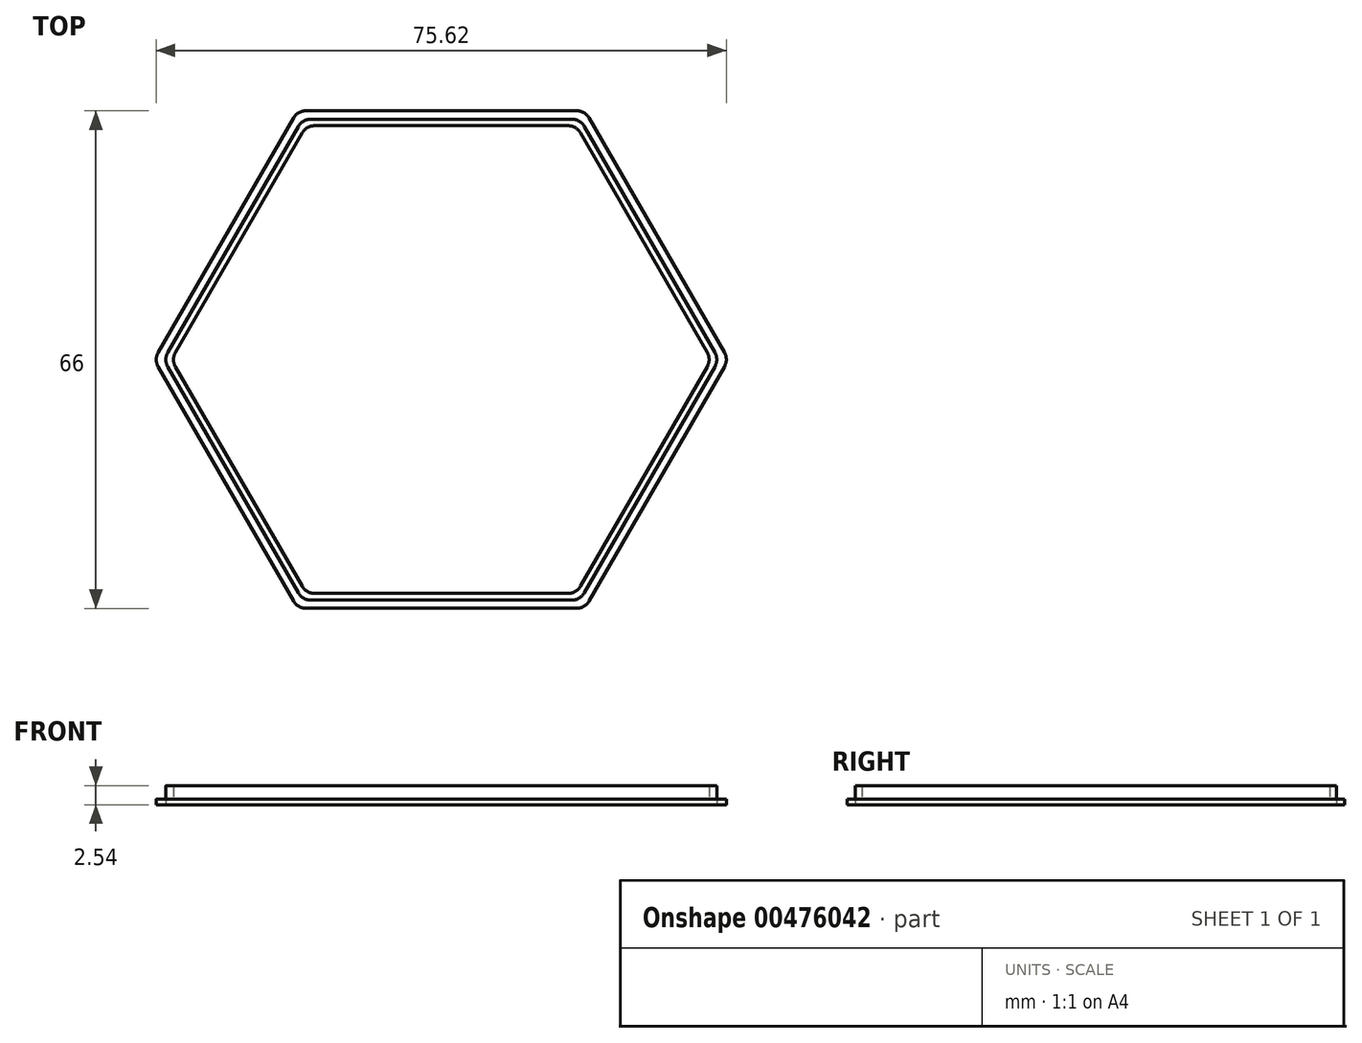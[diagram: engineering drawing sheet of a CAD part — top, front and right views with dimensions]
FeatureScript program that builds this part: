
annotation { "Feature Type Name" : "Feature", "Feature Type Description" : "" }
export const myFeature = defineFeature(function(context is Context, id is Id, definition is map)
    precondition{}
    {
        {
            var Q0;
            Q0=qCreatedBy(makeId("Top.planeOp"),FACE);
            var sketch = newSketch(context, id + "F0", { "sketchPlane" : qUnion([Q0])});
            skLineSegment(sketch, "E0", {"start": v(-56.1, -68.55) * mm, "end": v(58.07, -68.55) * mm});
            skLineSegment(sketch, "E1", {"start": v(0, 0) * mm, "end": v(-19.05, 33) * mm, "construction": true});
            skLineSegment(sketch, "E2", {"start": v(19.05, 33) * mm, "end": v(0, 0) * mm, "construction": true});
            skLineSegment(sketch, "E3", {"start": v(-19.05, 33) * mm, "end": v(19.05, 33) * mm});
            skLineSegment(sketch, "E4.1.0", {"start": v(-38.1, 0) * mm, "end": v(-19.05, 33) * mm});
            skLineSegment(sketch, "E4.2.0", {"start": v(-19.05, -33) * mm, "end": v(-38.1, 0) * mm});
            skLineSegment(sketch, "E4.3.0", {"start": v(19.05, -33) * mm, "end": v(-19.05, -33) * mm});
            skLineSegment(sketch, "E4.4.0", {"start": v(38.1, 0) * mm, "end": v(19.05, -33) * mm});
            skLineSegment(sketch, "E4.5.0", {"start": v(19.05, 33) * mm, "end": v(38.1, 0) * mm});
            skPoint(sketch, "E4.center", {"position": v(0, 0) * mm});
            skSolve(sketch);
        }
        {
            var Q0;
            Q0=makeQuery(id+"F0.imprint","IMPRINT",FACE,{"disambiguationData":[TD([[makeQuery(id+"F0.imprint","IMPRINT",EDGE,{"derivedFrom":sQuery(id+"F0.wireOp",EDGE,"E3")}),-1.0]])]});
            extrude(context, id + "F1", {"entities" : qUnion([Q0]), "depth" : 0.76 * mm, "offsetDistance" : 25.4 * mm});
        }
        {
            var Q0;
            Q0=makeQuery(id+"FdZoSmRdGPEDfu0_1.splitOp","SPLIT",EDGE,{"derivedFrom":makeQuery(id+"F1.opExtrude","SWEPT_EDGE",EDGE,{"disambiguationData":[OSD([sQuery(id+"F0.wireOp",EDGE,"E4.4.0"),sQuery(id+"F0.wireOp",EDGE,"E4.5.0")])]})});
            var Q1;
            Q1=makeQuery(id+"FdZoSmRdGPEDfu0_1.splitOp","SPLIT",EDGE,{"derivedFrom":makeQuery(id+"F1.opExtrude","SWEPT_EDGE",EDGE,{"disambiguationData":[OSD([sQuery(id+"F0.wireOp",EDGE,"E3"),sQuery(id+"F0.wireOp",EDGE,"E4.5.0")])]})});
            var Q2;
            Q2=makeQuery(id+"FdZoSmRdGPEDfu0_1.splitOp","SPLIT",EDGE,{"derivedFrom":makeQuery(id+"F1.opExtrude","SWEPT_EDGE",EDGE,{"disambiguationData":[OSD([sQuery(id+"F0.wireOp",EDGE,"E3"),sQuery(id+"F0.wireOp",EDGE,"E4.1.0")])]})});
            var Q3;
            Q3=makeQuery(id+"FdZoSmRdGPEDfu0_1.splitOp","SPLIT",EDGE,{"derivedFrom":makeQuery(id+"F1.opExtrude","SWEPT_EDGE",EDGE,{"disambiguationData":[OSD([sQuery(id+"F0.wireOp",EDGE,"E4.1.0"),sQuery(id+"F0.wireOp",EDGE,"E4.2.0")])]})});
            var Q4;
            Q4=makeQuery(id+"FdZoSmRdGPEDfu0_1.splitOp","SPLIT",EDGE,{"derivedFrom":makeQuery(id+"F1.opExtrude","SWEPT_EDGE",EDGE,{"disambiguationData":[OSD([sQuery(id+"F0.wireOp",EDGE,"E4.2.0"),sQuery(id+"F0.wireOp",EDGE,"E4.3.0")])]})});
            var Q5;
            Q5=makeQuery(id+"FdZoSmRdGPEDfu0_1.splitOp","SPLIT",EDGE,{"derivedFrom":makeQuery(id+"F1.opExtrude","SWEPT_EDGE",EDGE,{"disambiguationData":[OSD([sQuery(id+"F0.wireOp",EDGE,"E4.3.0"),sQuery(id+"F0.wireOp",EDGE,"E4.4.0")])]})});
            fillet(context, id + "F2", {"entities" : qUnion([Q0, Q1, Q2, Q3, Q4, Q5]), "radius" : 1.9 * mm, "allowEdgeOverflow" : false});
        }
        {
            var Q0;
            Q0=qCreatedBy(makeId("Top.planeOp"),FACE);
            var sketch = newSketch(context, id + "F3", { "sketchPlane" : qUnion([Q0])});
            skLineSegment(sketch, "E5", {"start": v(0, 0) * mm, "end": v(-18.41, 31.9) * mm, "construction": true});
            skLineSegment(sketch, "E6", {"start": v(0, 0) * mm, "end": v(18.41, 31.9) * mm, "construction": true});
            skLineSegment(sketch, "E7", {"start": v(-18.41, 31.9) * mm, "end": v(18.41, 31.9) * mm});
            skLineSegment(sketch, "E8.1.0", {"start": v(-36.83, 0) * mm, "end": v(-18.41, 31.9) * mm});
            skLineSegment(sketch, "E8.2.0", {"start": v(-18.42, -31.9) * mm, "end": v(-36.83, 0) * mm});
            skLineSegment(sketch, "E8.3.0", {"start": v(18.41, -31.9) * mm, "end": v(-18.41, -31.9) * mm});
            skLineSegment(sketch, "E8.4.0", {"start": v(36.83, 0) * mm, "end": v(18.41, -31.9) * mm});
            skLineSegment(sketch, "E8.5.0", {"start": v(18.41, 31.9) * mm, "end": v(36.83, 0) * mm});
            skPoint(sketch, "E8.center", {"position": v(0, 0) * mm});
            skSolve(sketch);
        }
        {
            var Q0;
            Q0=qSketchRegion(id+"F3",true);
            extrude(context, id + "F4", {"entities" : qUnion([Q0]), "depth" : 2.54 * mm, "offsetDistance" : 25.4 * mm});
        }
        {
            var Q0;
            Q0=makeQuery(id+"F4.opExtrude","SWEPT_EDGE",EDGE,{"disambiguationData":[OSD([sQuery(id+"F3.wireOp",EDGE,"E8.2.0"),sQuery(id+"F3.wireOp",EDGE,"E8.3.0")])]});
            var Q1;
            Q1=makeQuery(id+"F4.opExtrude","SWEPT_EDGE",EDGE,{"disambiguationData":[OSD([sQuery(id+"F3.wireOp",EDGE,"E8.3.0"),sQuery(id+"F3.wireOp",EDGE,"E8.4.0")])]});
            var Q2;
            Q2=makeQuery(id+"F4.opExtrude","SWEPT_EDGE",EDGE,{"disambiguationData":[OSD([sQuery(id+"F3.wireOp",EDGE,"E8.4.0"),sQuery(id+"F3.wireOp",EDGE,"E8.5.0")])]});
            var Q3;
            Q3=makeQuery(id+"F4.opExtrude","SWEPT_EDGE",EDGE,{"disambiguationData":[OSD([sQuery(id+"F3.wireOp",EDGE,"E8.1.0"),sQuery(id+"F3.wireOp",EDGE,"E8.2.0")])]});
            var Q4;
            Q4=makeQuery(id+"F4.opExtrude","SWEPT_EDGE",EDGE,{"disambiguationData":[OSD([sQuery(id+"F3.wireOp",EDGE,"E7"),sQuery(id+"F3.wireOp",EDGE,"E8.5.0")])]});
            var Q5;
            Q5=makeQuery(id+"F4.opExtrude","SWEPT_EDGE",EDGE,{"disambiguationData":[OSD([sQuery(id+"F3.wireOp",EDGE,"E7"),sQuery(id+"F3.wireOp",EDGE,"E8.1.0")])]});
            fillet(context, id + "F5", {"entities" : qUnion([Q0, Q1, Q2, Q3, Q4, Q5]), "radius" : 1.9 * mm, "tangentPropagation" : true, "allowEdgeOverflow" : false});
        }
        {
            var Q0;
            Q0=qCreatedBy(makeId("Top.planeOp"),FACE);
            var sketch = newSketch(context, id + "F6", { "sketchPlane" : qUnion([Q0])});
            skLineSegment(sketch, "E9", {"start": v(-17.9, 31.02) * mm, "end": v(0, 0) * mm, "construction": true});
            skLineSegment(sketch, "E10", {"start": v(0, 0) * mm, "end": v(17.9, 31.02) * mm, "construction": true});
            skLineSegment(sketch, "E11", {"start": v(-17.9, 31.02) * mm, "end": v(17.9, 31.02) * mm});
            skLineSegment(sketch, "E12.1.0", {"start": v(-35.81, 0) * mm, "end": v(-17.9, 31.02) * mm});
            skLineSegment(sketch, "E12.2.0", {"start": v(-17.9, -31.02) * mm, "end": v(-35.81, 0) * mm});
            skLineSegment(sketch, "E12.3.0", {"start": v(17.9, -31.02) * mm, "end": v(-17.9, -31.02) * mm});
            skLineSegment(sketch, "E12.4.0", {"start": v(35.81, 0) * mm, "end": v(17.9, -31.02) * mm});
            skLineSegment(sketch, "E12.5.0", {"start": v(17.9, 31.02) * mm, "end": v(35.81, 0) * mm});
            skPoint(sketch, "E12.center", {"position": v(0, 0) * mm});
            skSolve(sketch);
        }
        {
            var Q0;
            Q0 = qSketchRegion(id + "F6", true);
            extrude(context, id + "F7", {"entities" : qUnion([Q0]), "depth" : 2.54 * mm, "offsetDistance" : 25.4 * mm});
        }
        {
            var Q0;
            Q0=makeQuery(id+"F7.opExtrude","SWEPT_EDGE",EDGE,{"disambiguationData":[OSD([sQuery(id+"F6.wireOp",EDGE,"E12.2.0"),sQuery(id+"F6.wireOp",EDGE,"E12.3.0")])]});
            var Q1;
            Q1=makeQuery(id+"F7.opExtrude","SWEPT_EDGE",EDGE,{"disambiguationData":[OSD([sQuery(id+"F6.wireOp",EDGE,"E12.3.0"),sQuery(id+"F6.wireOp",EDGE,"E12.4.0")])]});
            var Q2;
            Q2=makeQuery(id+"F7.opExtrude","SWEPT_EDGE",EDGE,{"disambiguationData":[OSD([sQuery(id+"F6.wireOp",EDGE,"E12.4.0"),sQuery(id+"F6.wireOp",EDGE,"E12.5.0")])]});
            var Q3;
            Q3=makeQuery(id+"F7.opExtrude","SWEPT_EDGE",EDGE,{"disambiguationData":[OSD([sQuery(id+"F6.wireOp",EDGE,"E12.1.0"),sQuery(id+"F6.wireOp",EDGE,"E12.2.0")])]});
            var Q4;
            Q4=makeQuery(id+"F7.opExtrude","SWEPT_EDGE",EDGE,{"disambiguationData":[OSD([sQuery(id+"F6.wireOp",EDGE,"E11"),sQuery(id+"F6.wireOp",EDGE,"E12.5.0")])]});
            var Q5;
            Q5=makeQuery(id+"F7.opExtrude","SWEPT_EDGE",EDGE,{"disambiguationData":[OSD([sQuery(id+"F6.wireOp",EDGE,"E11"),sQuery(id+"F6.wireOp",EDGE,"E12.1.0")])]});
            fillet(context, id + "F8", {"entities" : qUnion([Q0, Q1, Q2, Q3, Q4, Q5]), "radius" : 1.9 * mm, "tangentPropagation" : true, "allowEdgeOverflow" : false});
        }
        {
            var Q0;
            Q0=makeQuery(id+"F7.opExtrude","SWEPT_BODY",BODY,{"disambiguationData":[OSD([sQuery(id+"F6.wireOp",EDGE,"E11"),sQuery(id+"F6.wireOp",EDGE,"E12.1.0"),sQuery(id+"F6.wireOp",EDGE,"E12.2.0"),sQuery(id+"F6.wireOp",EDGE,"E12.3.0"),sQuery(id+"F6.wireOp",EDGE,"E12.4.0"),sQuery(id+"F6.wireOp",EDGE,"E12.5.0")])]});
            transform(context, id + "F9", {"entities" : qUnion([Q0]), "transformType" : TransformType.TRANSLATION_3D, "dx" : 0 * mm, "dy" : 0 * mm, "dz" : 0.76 * mm, "makeCopy" : false});
        }
        {
            var Q0;
            Q0=makeQuery(id+"F7.opExtrude","SWEPT_BODY",BODY,{"disambiguationData":[OSD([sQuery(id+"F6.wireOp",EDGE,"E11"),sQuery(id+"F6.wireOp",EDGE,"E12.1.0"),sQuery(id+"F6.wireOp",EDGE,"E12.2.0"),sQuery(id+"F6.wireOp",EDGE,"E12.3.0"),sQuery(id+"F6.wireOp",EDGE,"E12.4.0"),sQuery(id+"F6.wireOp",EDGE,"E12.5.0")])]});
            var Q1;
            Q1=makeQuery(id+"F4.opExtrude","SWEPT_BODY",BODY,{"disambiguationData":[OSD([sQuery(id+"F3.wireOp",EDGE,"E7"),sQuery(id+"F3.wireOp",EDGE,"E8.1.0"),sQuery(id+"F3.wireOp",EDGE,"E8.2.0"),sQuery(id+"F3.wireOp",EDGE,"E8.3.0"),sQuery(id+"F3.wireOp",EDGE,"E8.4.0"),sQuery(id+"F3.wireOp",EDGE,"E8.5.0")])]});
            booleanBodies(context, id + "F10", {"operationType" : BooleanOperationType.SUBTRACTION, "tools" : qUnion([Q0]), "targets" : qUnion([Q1])});
        }
    });
